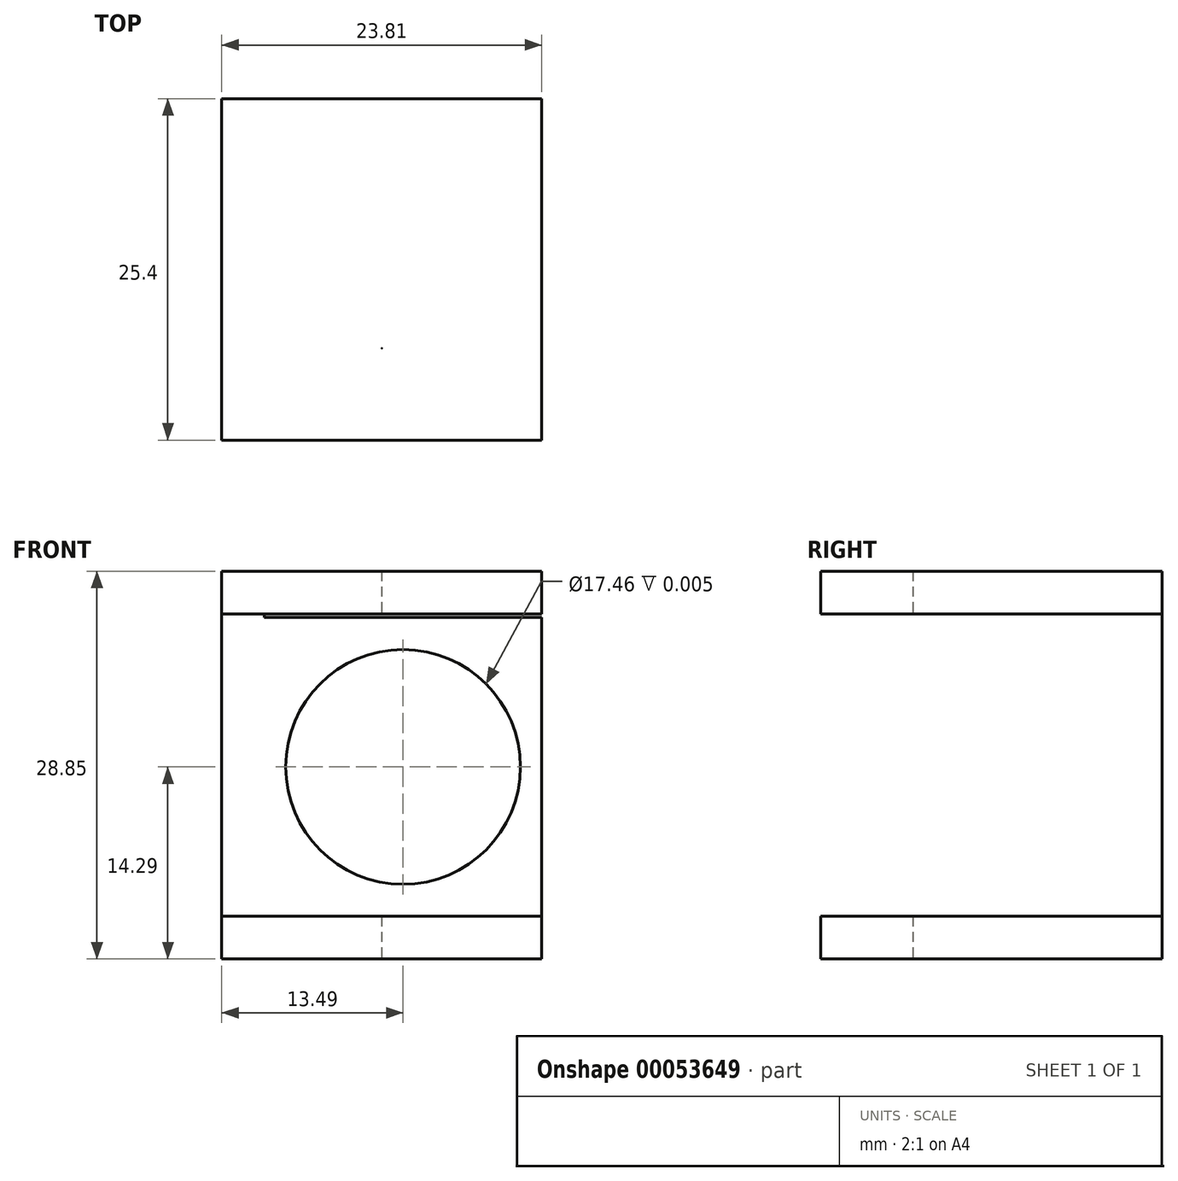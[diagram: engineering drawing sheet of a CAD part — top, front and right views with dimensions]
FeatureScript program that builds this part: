
annotation { "Feature Type Name" : "Feature", "Feature Type Description" : "" }
export const myFeature = defineFeature(function(context is Context, id is Id, definition is map)
    precondition{}
    {
        {
            var Q0;
            Q0=qCreatedBy(makeId("Front.planeOp"),FACE);
            var sketch = newSketch(context, id + "F0", { "sketchPlane" : qUnion([Q0])});
            skLineSegment(sketch, "E0.rect.bottom", {"start": v(10.32, 11.11) * mm, "end": v(-10.32, 11.11) * mm});
            skLineSegment(sketch, "E0.rect.top", {"start": v(10.32, -11.11) * mm, "end": v(-10.32, -11.11) * mm});
            skLineSegment(sketch, "E0.rect.left", {"start": v(10.32, 11.11) * mm, "end": v(10.32, -11.11) * mm});
            skLineSegment(sketch, "E0.rect.right", {"start": v(-10.32, 11.11) * mm, "end": v(-10.32, -11.11) * mm});
            skPoint(sketch, "E0.rect.middle", {"position": v(0, 0) * mm});
            skLineSegment(sketch, "E1.bottom", {"start": v(-10.32, -11.11) * mm, "end": v(-13.5, -11.11) * mm});
            skLineSegment(sketch, "E1.top", {"start": v(-10.32, 11.39) * mm, "end": v(-13.5, 11.39) * mm});
            skLineSegment(sketch, "E1.left", {"start": v(-10.32, -11.11) * mm, "end": v(-10.32, 11.39) * mm});
            skLineSegment(sketch, "E1.right", {"start": v(-13.5, -11.11) * mm, "end": v(-13.5, 11.39) * mm});
            skCircle(sketch, "E2", {"center": v(0, 0) * mm, "radius": 8.73 * mm});
            skLineSegment(sketch, "E3.bottom", {"start": v(-13.5, -11.11) * mm, "end": v(10.32, -11.11) * mm});
            skLineSegment(sketch, "E3.top", {"start": v(-13.5, -14.29) * mm, "end": v(10.32, -14.29) * mm});
            skLineSegment(sketch, "E3.left", {"start": v(-13.5, -11.11) * mm, "end": v(-13.5, -14.29) * mm});
            skLineSegment(sketch, "E3.right", {"start": v(10.32, -11.11) * mm, "end": v(10.32, -14.29) * mm});
            skLineSegment(sketch, "E4.bottom", {"start": v(-13.5, 11.39) * mm, "end": v(10.32, 11.39) * mm});
            skLineSegment(sketch, "E4.top", {"start": v(-13.5, 14.56) * mm, "end": v(10.32, 14.56) * mm});
            skLineSegment(sketch, "E4.left", {"start": v(-13.5, 11.39) * mm, "end": v(-13.5, 14.56) * mm});
            skLineSegment(sketch, "E4.right", {"start": v(10.32, 11.39) * mm, "end": v(10.32, 14.56) * mm});
            skSolve(sketch);
        }
        {
            var Q0;
            {var subQ1=sQuery(id+"F0.wireOp",EDGE,"E0.rect.bottom");Q0=makeQuery(id+"F0.imprint","IMPRINT",FACE,{"disambiguationData":[TD([[makeQuery(id+"F0.imprint","IMPRINT",EDGE,{"derivedFrom":subQ1}),1.0]])]});}
            var Q1;
            {var subQ3=sQuery(id+"F0.wireOp",EDGE,"E1.right");Q1=makeQuery(id+"F0.imprint","IMPRINT",FACE,{"disambiguationData":[TD([[makeQuery(id+"F0.imprint","IMPRINT",EDGE,{"derivedFrom":subQ3}),-1.0]])]});}
            extrude(context, id + "F1", {"entities" : qUnion([Q0, Q1]), "depth" : 1 / 203.2 * mm});
        }
        {
            var Q0;
            Q0=makeQuery(id+"F0.imprint","IMPRINT",FACE,{"disambiguationData":[TD([[makeQuery(id+"F0.imprint","IMPRINT",EDGE,{"derivedFrom":sQuery(id+"F0.wireOp",EDGE,"E3.top")}),1.0]])]});
            var Q1;
            Q1=makeQuery(id+"F0.imprint","IMPRINT",FACE,{"disambiguationData":[TD([[makeQuery(id+"F0.imprint","IMPRINT",EDGE,{"derivedFrom":sQuery(id+"F0.wireOp",EDGE,"E4.top")}),-1.0]])]});
            extrude(context, id + "F2", {"entities" : qUnion([Q0, Q1]), "operationType" : NewBodyOperationType.ADD, "depth" : 25.4 * mm});
        }
        {
            var Q0;
            Q0=makeQuery(id+"F2.opExtrude","SWEPT_FACE",FACE,{"disambiguationData":[OSD([sQuery(id+"F0.wireOp",EDGE,"E3.top")])]});
            var sketch = newSketch(context, id + "F3", { "sketchPlane" : qUnion([Q0])});
            skLineSegment(sketch, "E5.bottom", {"start": v(-13.5, 0) * mm, "end": v(10.32, 0) * mm});
            skLineSegment(sketch, "E5.top", {"start": v(-13.5, 25.4) * mm, "end": v(10.32, 25.4) * mm});
            skLineSegment(sketch, "E5.left", {"start": v(-13.5, 0) * mm, "end": v(-13.5, 25.4) * mm});
            skLineSegment(sketch, "E5.right", {"start": v(10.32, 0) * mm, "end": v(10.32, 25.4) * mm});
            skLineSegment(sketch, "E6", {"start": v(-13.5, 18.56) * mm, "end": v(10.32, 18.56) * mm});
            skLineSegment(sketch, "E7", {"start": v(10.32, 18.56) * mm, "end": v(-1.59, 18.56) * mm});
            skLineSegment(sketch, "E8", {"start": v(-1.59, 18.56) * mm, "end": v(10.32, 18.56) * mm});
            skCircle(sketch, "E9", {"center": v(-1.59, 18.56) * mm, "radius": 3.57 * mm});
            skLineSegment(sketch, "E10", {"start": v(10.32, 0) * mm, "end": v(10.32, 18.56) * mm});
            skLineSegment(sketch, "E11", {"start": v(-1.59, 14.99) * mm, "end": v(-1.59, 0) * mm});
            skPoint(sketch, "E11.startSnap0", {"position": v(-1.59, 0) * mm});
            skLineSegment(sketch, "E12", {"start": v(-1.59, 0) * mm, "end": v(-1.59, 14.99) * mm});
            skSolve(sketch);
        }
        {
            var Q0;
            Q0=sQuery(id+"F3.wireOp",VERTEX,"E9.center");
            var Q1;
            Q1=makeQuery(id+"F1.opExtrude","SWEPT_BODY",BODY,{"disambiguationData":[OSD([sQuery(id+"F0.wireOp",EDGE,"E0.rect.bottom"),sQuery(id+"F0.wireOp",EDGE,"E0.rect.left"),sQuery(id+"F0.wireOp",EDGE,"E1.left"),sQuery(id+"F0.wireOp",EDGE,"E1.right"),sQuery(id+"F0.wireOp",EDGE,"E2"),sQuery(id+"F0.wireOp",EDGE,"E3.bottom"),sQuery(id+"F0.wireOp",EDGE,"E4.bottom")])]});
            hole(context, id + "F4", {"style" : HoleStyle.SIMPLE, "holeDiameter" : 9 / 812.8 * mm, "endStyle" : HoleEndStyle.THROUGH, "locations" : qUnion([Q0]), "scope" : qUnion([Q1])});
        }
    });
